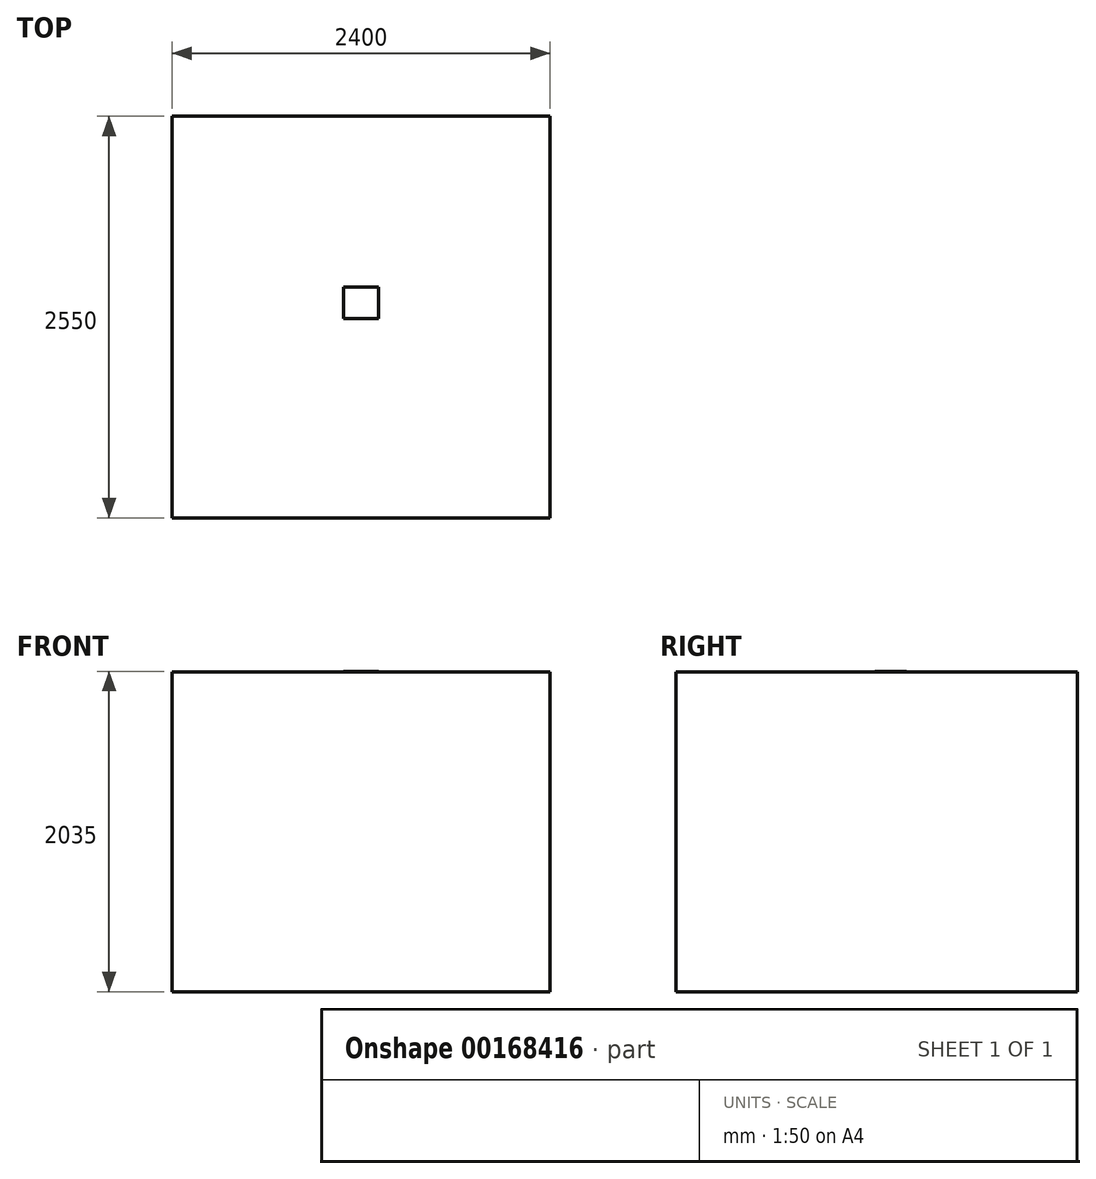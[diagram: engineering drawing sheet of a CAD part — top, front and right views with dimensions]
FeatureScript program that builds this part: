
annotation { "Feature Type Name" : "Feature", "Feature Type Description" : "" }
export const myFeature = defineFeature(function(context is Context, id is Id, definition is map)
    precondition{}
    {
        {
            var Q0;
            Q0=qCreatedBy(makeId("Top.planeOp"),FACE);
            var sketch = newSketch(context, id + "F0", { "sketchPlane" : qUnion([Q0])});
            skLineSegment(sketch, "E0.bottom", {"start": v(1200, 1275) * mm, "end": v(-1200, 1275) * mm});
            skLineSegment(sketch, "E0.top", {"start": v(1200, -1275) * mm, "end": v(-1200, -1275) * mm});
            skLineSegment(sketch, "E0.left", {"start": v(1200, 1275) * mm, "end": v(1200, -1275) * mm});
            skLineSegment(sketch, "E0.right", {"start": v(-1200, 1275) * mm, "end": v(-1200, -1275) * mm});
            skPoint(sketch, "E0.middle", {"position": v(0, 0) * mm});
            skSolve(sketch);
        }
        {
            var Q0;
            Q0 = qSketchRegion(id + "F0", true);
            extrude(context, id + "F2", {"entities" : qUnion([Q0]), "depth" : 2030 * mm});
        }
        {
            var Q0;
            Q0=makeQuery(id+"F2.opExtrude","CAP_FACE",FACE,{"disambiguationData":[OSD([sQuery(id+"F0.wireOp",EDGE,"E0.bottom"),sQuery(id+"F0.wireOp",EDGE,"E0.top"),sQuery(id+"F0.wireOp",EDGE,"E0.left"),sQuery(id+"F0.wireOp",EDGE,"E0.right")])],"isStart":false});
            var sketch = newSketch(context, id + "F1", { "sketchPlane" : qUnion([Q0])});
            skLineSegment(sketch, "E1.bottom", {"start": v(110, 189.59) * mm, "end": v(-110, 189.59) * mm});
            skLineSegment(sketch, "E1.top", {"start": v(110, -10.41) * mm, "end": v(-110, -10.41) * mm});
            skLineSegment(sketch, "E1.left", {"start": v(110, 189.59) * mm, "end": v(110, -10.41) * mm});
            skLineSegment(sketch, "E1.right", {"start": v(-110, 189.59) * mm, "end": v(-110, -10.41) * mm});
            skPoint(sketch, "E1.middle", {"position": v(0, 89.59) * mm});
            skSolve(sketch);
        }
        {
            var Q0;
            Q0=makeQuery(id+"F1.imprint","IMPRINT",FACE,{"disambiguationData":[TD([[makeQuery(id+"F1.imprint","IMPRINT",EDGE,{"derivedFrom":sQuery(id+"F1.wireOp",EDGE,"E1.bottom")}),1.0]])]});
            extrude(context, id + "F3", {"entities" : qUnion([Q0]), "depth" : 5 * mm});
        }
    });
